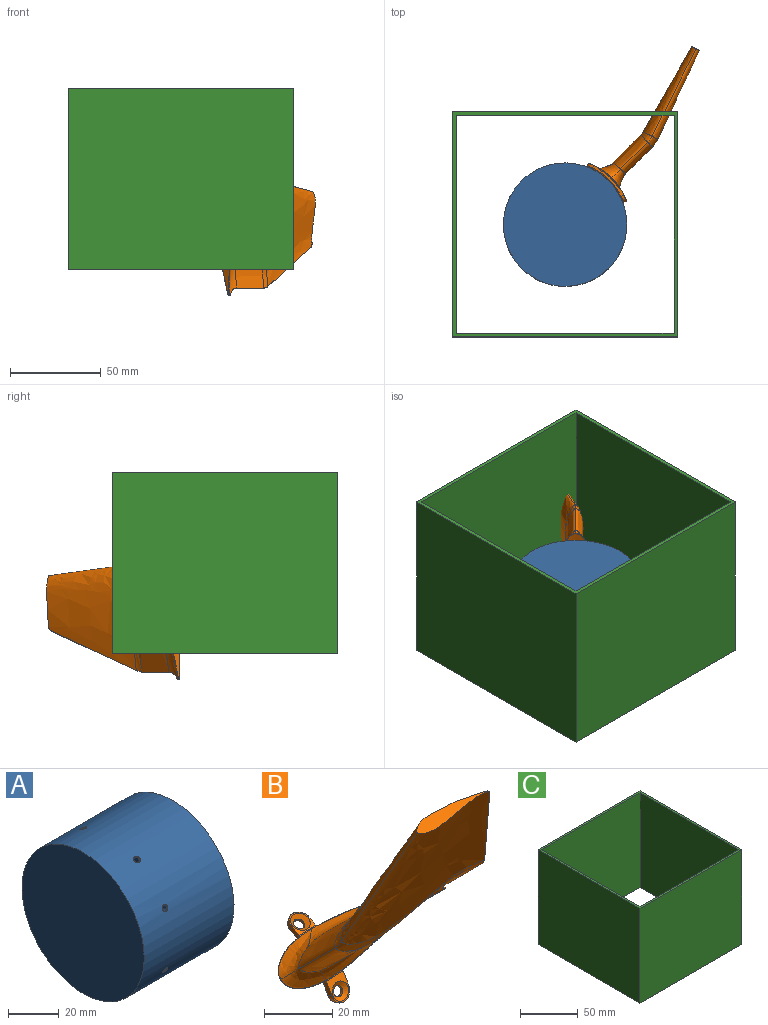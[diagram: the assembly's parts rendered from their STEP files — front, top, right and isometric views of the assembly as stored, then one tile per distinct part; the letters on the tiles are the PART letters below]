
ASSEMBLY  parts=3 mates=2
PART A: 27 faces, bbox 50x68x68 mm
  f0: plane 2.31x2.08mm, normal (0,0.9,0.44), area 4.2mm2, adj f8
  f1: plane 2.31x2.08mm, normal (0,0.44,0.9), area 4.2mm2, adj f9
  f2: plane 2.31x2.08mm, normal (0,0.44,-0.9), area 4.2mm2, adj f10
  f3: plane 2.31x2.08mm, normal (0,0.9,-0.44), area 4.2mm2, adj f11
  f4: plane 2.31x2.08mm, normal (0,-0.44,0.9), area 4.2mm2, adj f12
  f5: plane 2.31x2.08mm, normal (0,-0.9,0.44), area 4.2mm2, adj f13
  f6: plane 2.31x2.08mm, normal (0,-0.9,-0.44), area 4.2mm2, adj f14
  f7: plane 2.31x2.08mm, normal (0,-0.44,-0.9), area 4.2mm2, adj f15
  f8: cylinder r=1.16mm len=7.89mm, axis (0,-0.9,-0.44), area 55.6mm2, adj f0,f16
  f9: cylinder r=1.16mm len=7.89mm, axis (0,-0.44,-0.9), area 55.6mm2, adj f1,f17
  f10: cylinder r=1.16mm len=7.89mm, axis (0,-0.44,0.9), area 55.6mm2, adj f2,f18
  f11: cylinder r=1.16mm len=7.89mm, axis (0,-0.9,0.44), area 55.6mm2, adj f3,f19
  f12: cylinder r=1.16mm len=7.89mm, axis (0,-0.44,0.9), area 55.6mm2, adj f4,f21
  f13: cylinder r=1.16mm len=7.89mm, axis (0,-0.9,0.44), area 55.6mm2, adj f5,f22
  f14: cylinder r=1.16mm len=7.89mm, axis (0,-0.9,-0.44), area 55.6mm2, adj f6,f23
  f15: cylinder r=1.16mm len=7.89mm, axis (0,-0.44,-0.9), area 55.6mm2, adj f7,f24
  f16: cone r=0mm half-angle=45deg, axis (0,0.9,0.44), area 3.9mm2, adj f8,f25
  f17: cone r=0mm half-angle=45deg, axis (0,0.44,0.9), area 3.9mm2, adj f9,f25
  f18: cone r=0mm half-angle=45deg, axis (0,0.44,-0.9), area 3.9mm2, adj f10,f25
  f19: cone r=0mm half-angle=45deg, axis (0,0.9,-0.44), area 3.9mm2, adj f11,f25
  f20: plane 68x68mm, normal (1,0,0), area 3631.7mm2, adj f25
  f21: cone r=0mm half-angle=45deg, axis (0,-0.44,0.9), area 3.9mm2, adj f12,f25
  f22: cone r=0mm half-angle=45deg, axis (0,-0.9,0.44), area 3.9mm2, adj f13,f25
  f23: cone r=0mm half-angle=45deg, axis (0,-0.9,-0.44), area 3.9mm2, adj f14,f25
  f24: cone r=0mm half-angle=45deg, axis (0,-0.44,-0.9), area 3.9mm2, adj f15,f25
  f25: cylinder r=34mm len=68mm, axis (1,0,0), area 10626.9mm2, adj f16,f17,f18,f19,f20,f21,f22,f23
  f26: plane 68x68mm, normal (-1,0,0), area 3631.7mm2, adj f25
PART B: 49 faces, bbox 70x62x85.9 mm
  f0: cylinder r=1.7mm len=3.44mm, axis (0,0.44,-0.9), area 9.3mm2, adj f2,f3
  f1: cylinder r=1.7mm len=3.44mm, axis (0,0.9,-0.44), area 9.3mm2, adj f3,f6
  f2: cone r=0mm half-angle=50deg, axis (0,-0.44,0.9), area 24mm2, adj f0,f11
  f3: cylinder r=34mm len=19.43mm, axis (-1,0,0), area 149.1mm2, adj f0,f1,f4,f5,f9,f13
  f4: bspline ~7x3.34mm, area 6.7mm2, adj f3,f9,f12,f13
  f5: bspline ~7x3.34mm, area 6.7mm2, adj f3,f9,f13,f14
  f6: cone r=0mm half-angle=50deg, axis (0,-0.9,0.44), area 24mm2, adj f1,f15
  f7: cylinder r=36mm len=13.81mm, axis (-1,0,0), area 101.3mm2, adj f8,f20,f24
  f8: torus R=35.5mm, axis (-1,0,0), area 12.1mm2, adj f7,f21,f23,f26
  f9: torus R=34.4mm, axis (-1,0,0), area 14mm2, adj f3,f4,f5,f26
  f10: torus R=35.5mm, axis (-1,0,0), area 12mm2, adj f16,f17,f28,f29
  f11: cylinder r=36mm len=7mm, axis (-1,0,0), area 13.7mm2, adj f2,f12,f19,f22,f26,f29
  f12: cylinder r=3.5mm len=7mm, axis (0,0.35,-0.94), area 17.7mm2, adj f4,f11,f26,f29
  f13: torus R=34.4mm, axis (-1,0,0), area 14mm2, adj f3,f4,f5,f29
  f14: cylinder r=3.5mm len=7mm, axis (0,-0.94,0.35), area 17.7mm2, adj f5,f15,f26,f29
  f15: cylinder r=36mm len=7.51mm, axis (-1,0,0), area 23.8mm2, adj f6,f14,f25,f26,f29,f30
  f16: cylinder r=36mm len=44.99mm, axis (-1,0,0), area 364.4mm2, adj f10,f18,f27,f32
  f17: bspline ~1x0.68mm, area 0.2mm2, adj f10,f18,f29,f34
  f18: bspline ~45.79x6.89mm, area 10.1mm2, adj f16,f17,f32,f34
  f19: cylinder r=0.5mm len=1.78mm, axis (1,0,0), area 0.6mm2, adj f11,f22,f29,f34
  f20: bspline ~14.09x6.47mm, area 4.2mm2, adj f7,f21,f24,f35
  f21: bspline ~1.1x0.69mm, area 0.2mm2, adj f8,f20,f26,f35
  f22: bspline ~5.36x0.52mm, area 1.8mm2, adj f11,f19,f26,f35
  f23: bspline ~0.89x0.67mm, area 0.2mm2, adj f8,f24,f26,f36
  f24: bspline ~13.91x5.48mm, area 3.8mm2, adj f7,f20,f23,f36
  f25: cylinder r=0.5mm len=0.37mm, axis (1,-0.01,-0.01), area 0.1mm2, adj f15,f26,f30,f36
  f26: plane 17.17x17.17mm, normal (-1,0,0), area 29.1mm2, adj f8,f9,f11,f12,f14,f15,f21,f22
  f27: bspline ~45.06x4.41mm, area 8.1mm2, adj f16,f28,f32,f37
  f28: bspline ~0.9x0.68mm, area 0.2mm2, adj f10,f27,f29,f37
  f29: plane 17.16x17.16mm, normal (1,0,0), area 29.2mm2, adj f10,f11,f12,f13,f14,f15,f17,f19
  f30: bspline ~6.86x0.63mm, area 2.7mm2, adj f15,f25,f29,f37
  f31: cylinder r=0.5mm len=0.74mm, axis (0,0.69,0.72), area 0.2mm2, adj f32,f33,f34,f37
  f32: cylinder r=66.37mm len=0.96mm, axis (-0.27,0.71,-0.66), area 0.4mm2, adj f16,f18,f27,f31,f34,f37
  f33: bspline ~5.02x4mm, area 2.2mm2, adj f31,f34,f37,f38
  f34: bspline ~60.46x11.86mm, area 396.6mm2, adj f17,f18,f19,f29,f31,f32,f33,f35
  f35: bspline ~20.33x11.76mm, area 119.6mm2, adj f20,f21,f22,f26,f34,f36,f39
  f36: bspline ~15.49x10.63mm, area 94.7mm2, adj f23,f24,f25,f26,f35,f37,f40
  f37: bspline ~61.09x11.04mm, area 407.8mm2, adj f27,f28,f29,f30,f31,f32,f33,f36
  f38: plane 15.07x15.07mm, normal (1,0,0), area 6.3mm2, adj f33,f39,f40,f41
  f39: extruded ~60x18.66mm, area 1297.7mm2, adj f34,f35,f38,f40,f42
  f40: extruded ~60x18.09mm, area 1320.2mm2, adj f36,f37,f38,f39,f43
  f41: cylinder r=10.54mm len=3.81mm, axis (0,0.87,0.5), area 1.2mm2, adj f38,f42,f43,f44
  f42: bspline ~60.61x6.16mm, area 173.1mm2, adj f39,f41,f43,f45
  f43: bspline ~60x6.28mm, area 276mm2, adj f40,f41,f42,f46
  f44: plane 46.61x23.95mm, normal (0.92,-0.17,0.34), area 16.9mm2, adj f41,f45,f46,f47
  f45: bspline ~59.52x49.34mm, area 2486.6mm2, adj f42,f44,f46,f47,f48
  f46: bspline ~58.93x50.01mm, area 2468.4mm2, adj f43,f44,f45,f47,f48
  f47: cylinder r=3mm len=2.77mm, axis (0,0.89,0.45), area 1.3mm2, adj f44,f45,f46,f48
  f48: plane 28.05x4.24mm, normal (0,-0.45,0.89), area 83mm2, adj f45,f46,f47
PART C: 10 faces, bbox 124x124x100 mm
  f0: plane 124x124mm, normal (0,0,1), area 976mm2, adj f1,f2,f3,f4,f5,f6,f7,f8
  f1: plane 124x100mm, normal (-1,0,0), area 12400mm2, adj f0,f2,f4,f9
  f2: plane 124x100mm, normal (0,-1,0), area 12400mm2, adj f0,f1,f3,f9
  f3: plane 124x100mm, normal (1,0,0), area 12400mm2, adj f0,f2,f4,f9
  f4: plane 124x100mm, normal (0,1,0), area 12400mm2, adj f0,f1,f3,f9
  f5: plane 120x100mm, normal (0,-1,0), area 12000mm2, adj f0,f6,f8,f9
  f6: plane 120x100mm, normal (-1,0,0), area 12000mm2, adj f0,f5,f7,f9
  f7: plane 120x100mm, normal (0,1,0), area 12000mm2, adj f0,f6,f8,f9
  f8: plane 120x100mm, normal (1,0,0), area 12000mm2, adj f0,f5,f7,f9
  f9: plane 124x124mm, normal (0,0,-1), area 976mm2, adj f1,f2,f3,f4,f5,f6,f7,f8
PLACE A rot(axis=(0,1,0),90deg) t=(-4.78,65.89,-46.42)mm
PLACE B rot(axis=(-0.58,0.58,0.58),120deg) t=(-4.66,66.13,-46.42)mm
PLACE C t=(-4.78,65.89,-46.42)mm fixed
MATE fastened A.f25 <-> C.f9  axis (0,0,-1) through (-4.78,65.89,-96.42)mm
MATE fastened B.f0 <-> A.f16  axis (-0.44,-0.9,0) through (10.41,97.04,-61.42)mm
